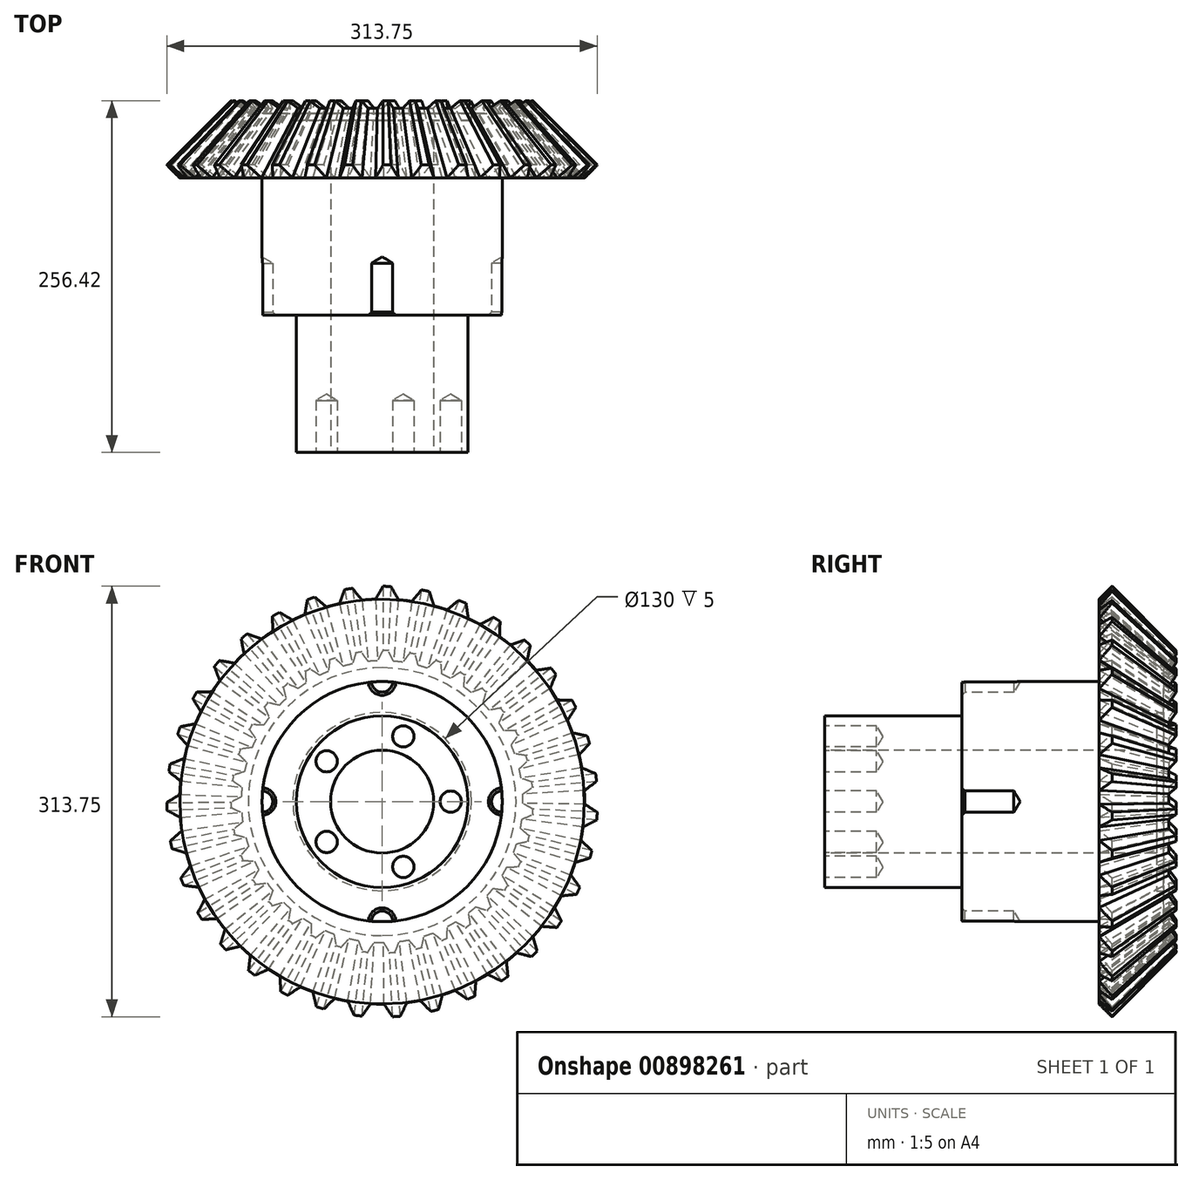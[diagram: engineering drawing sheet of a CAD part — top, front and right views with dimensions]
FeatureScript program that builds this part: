
annotation { "Feature Type Name" : "Feature", "Feature Type Description" : "" }
export const myFeature = defineFeature(function(context is Context, id is Id, definition is map)
    precondition{}
    {
        {
            var Q0;
            Q0=qCreatedBy(makeId("Front.planeOp"),FACE);
            var sketch = newSketch(context, id + "F0", { "sketchPlane" : qUnion([Q0])});
            skArc(sketch, "E0", {"start": v(-656.1, 368.1) * mm, "mid": v(-658.99, 367.13) * mm, "end": v(-661.85, 366.1) * mm});
            skLineSegment(sketch, "E1", {"start": v(-602.6, 62.21) * mm, "end": v(-595.9, 43.66) * mm});
            skLineSegment(sketch, "E2", {"start": v(-589.83, 44.07) * mm, "end": v(-586.01, 63.32) * mm});
            skLineSegment(sketch, "E3", {"start": v(-602.6, 62.21) * mm, "end": v(-604.03, 62.21) * mm});
            skLineSegment(sketch, "E4", {"start": v(-576.25, 64.84) * mm, "end": v(-566.34, 47.79) * mm});
            skLineSegment(sketch, "E5", {"start": v(-560.44, 49.27) * mm, "end": v(-560.12, 68.9) * mm});
            skLineSegment(sketch, "E6", {"start": v(-550.78, 72.14) * mm, "end": v(-537.98, 57.12) * mm});
            skLineSegment(sketch, "E7", {"start": v(-532.45, 59.64) * mm, "end": v(-535.64, 79) * mm});
            skLineSegment(sketch, "E8", {"start": v(-527.03, 83.86) * mm, "end": v(-511.75, 71.37) * mm});
            skLineSegment(sketch, "E9", {"start": v(-506.76, 74.83) * mm, "end": v(-513.35, 93.31) * mm});
            skLineSegment(sketch, "E10", {"start": v(-505.75, 99.63) * mm, "end": v(-488.5, 90.08) * mm});
            skLineSegment(sketch, "E11", {"start": v(-484.2, 94.37) * mm, "end": v(-493.98, 111.38) * mm});
            skLineSegment(sketch, "E12", {"start": v(-487.63, 118.96) * mm, "end": v(-468.94, 112.63) * mm});
            skLineSegment(sketch, "E13", {"start": v(-465.48, 117.63) * mm, "end": v(-478.14, 132.62) * mm});
            skLineSegment(sketch, "E14", {"start": v(-473.25, 141.2) * mm, "end": v(-453.73, 138.32) * mm});
            skLineSegment(sketch, "E15", {"start": v(-451.22, 143.85) * mm, "end": v(-466.36, 156.34) * mm});
            skLineSegment(sketch, "E16", {"start": v(-463.07, 165.66) * mm, "end": v(-443.36, 166.3) * mm});
            skLineSegment(sketch, "E17", {"start": v(-441.87, 172.2) * mm, "end": v(-459, 181.78) * mm});
            skLineSegment(sketch, "E18", {"start": v(-457.43, 191.54) * mm, "end": v(-438.14, 195.7) * mm});
            skLineSegment(sketch, "E19", {"start": v(-437.73, 201.76) * mm, "end": v(-456.3, 208.13) * mm});
            skLineSegment(sketch, "E20", {"start": v(-456.5, 218.01) * mm, "end": v(-438.26, 225.55) * mm});
            skLineSegment(sketch, "E21", {"start": v(-438.94, 231.59) * mm, "end": v(-458.34, 234.54) * mm});
            skLineSegment(sketch, "E22", {"start": v(-460.3, 244.23) * mm, "end": v(-443.7, 254.9) * mm});
            skLineSegment(sketch, "E23", {"start": v(-445.45, 260.72) * mm, "end": v(-465.07, 260.16) * mm});
            skLineSegment(sketch, "E24", {"start": v(-468.73, 269.34) * mm, "end": v(-454.3, 282.8) * mm});
            skLineSegment(sketch, "E25", {"start": v(-457.06, 288.22) * mm, "end": v(-476.26, 284.17) * mm});
            skLineSegment(sketch, "E26", {"start": v(-481.5, 292.55) * mm, "end": v(-469.72, 308.36) * mm});
            skLineSegment(sketch, "E27", {"start": v(-473.4, 313.2) * mm, "end": v(-491.57, 305.79) * mm});
            skLineSegment(sketch, "E28", {"start": v(-498.22, 313.1) * mm, "end": v(-489.45, 330.77) * mm});
            skLineSegment(sketch, "E29", {"start": v(-493.93, 334.87) * mm, "end": v(-510.48, 324.33) * mm});
            skLineSegment(sketch, "E30", {"start": v(-518.33, 330.33) * mm, "end": v(-512.86, 349.28) * mm});
            skLineSegment(sketch, "E31", {"start": v(-518, 352.52) * mm, "end": v(-532.4, 339.2) * mm});
            skLineSegment(sketch, "E32", {"start": v(-541.2, 343.7) * mm, "end": v(-539.2, 363.32) * mm});
            skLineSegment(sketch, "E33", {"start": v(-544.84, 365.59) * mm, "end": v(-556.63, 349.9) * mm});
            skLineSegment(sketch, "E34", {"start": v(-566.1, 352.77) * mm, "end": v(-567.62, 372.44) * mm});
            skLineSegment(sketch, "E35", {"start": v(-573.58, 373.66) * mm, "end": v(-582.38, 356.12) * mm});
            skLineSegment(sketch, "E36", {"start": v(-592.2, 357.25) * mm, "end": v(-597.22, 376.33) * mm});
            skLineSegment(sketch, "E37", {"start": v(-603.3, 376.46) * mm, "end": v(-608.83, 357.64) * mm});
            skLineSegment(sketch, "E38", {"start": v(-618.7, 357) * mm, "end": v(-627.03, 374.87) * mm});
            skLineSegment(sketch, "E39", {"start": v(-633.04, 373.92) * mm, "end": v(-635.12, 354.4) * mm});
            skLineSegment(sketch, "E40", {"start": v(-644.7, 352.01) * mm, "end": v(-656.1, 368.1) * mm});
            skLineSegment(sketch, "E41", {"start": v(-661.85, 366.1) * mm, "end": v(-660.4, 346.53) * mm});
            skLineSegment(sketch, "E42", {"start": v(-669.42, 342.47) * mm, "end": v(-683.51, 356.27) * mm});
            skLineSegment(sketch, "E43", {"start": v(-688.8, 353.27) * mm, "end": v(-683.89, 334.27) * mm});
            skLineSegment(sketch, "E44", {"start": v(-692.03, 328.66) * mm, "end": v(-708.36, 339.73) * mm});
            skLineSegment(sketch, "E45", {"start": v(-713.02, 335.83) * mm, "end": v(-704.8, 318.02) * mm});
            skLineSegment(sketch, "E46", {"start": v(-711.8, 311.04) * mm, "end": v(-729.85, 319.01) * mm});
            skLineSegment(sketch, "E47", {"start": v(-733.75, 314.35) * mm, "end": v(-722.48, 298.29) * mm});
            skLineSegment(sketch, "E48", {"start": v(-728.12, 290.17) * mm, "end": v(-747.3, 294.8) * mm});
            skLineSegment(sketch, "E49", {"start": v(-750.3, 289.5) * mm, "end": v(-736.34, 275.72) * mm});
            skLineSegment(sketch, "E50", {"start": v(-740.45, 266.73) * mm, "end": v(-760.14, 267.85) * mm});
            skLineSegment(sketch, "E51", {"start": v(-762.15, 262.11) * mm, "end": v(-745.96, 251.04) * mm});
            skLineSegment(sketch, "E52", {"start": v(-748.4, 241.46) * mm, "end": v(-767.97, 239.04) * mm});
            skLineSegment(sketch, "E53", {"start": v(-768.92, 233.04) * mm, "end": v(-751, 225.03) * mm});
            skLineSegment(sketch, "E54", {"start": v(-751.7, 215.17) * mm, "end": v(-770.53, 209.3) * mm});
            skLineSegment(sketch, "E55", {"start": v(-770.4, 203.23) * mm, "end": v(-751.34, 198.55) * mm});
            skLineSegment(sketch, "E56", {"start": v(-750.25, 188.72) * mm, "end": v(-767.73, 179.58) * mm});
            skLineSegment(sketch, "E57", {"start": v(-766.52, 173.63) * mm, "end": v(-746.93, 172.43) * mm});
            skLineSegment(sketch, "E58", {"start": v(-744.1, 162.95) * mm, "end": v(-759.68, 150.84) * mm});
            skLineSegment(sketch, "E59", {"start": v(-757.42, 145.2) * mm, "end": v(-737.93, 147.51) * mm});
            skLineSegment(sketch, "E60", {"start": v(-733.46, 138.7) * mm, "end": v(-746.62, 124) * mm});
            skLineSegment(sketch, "E61", {"start": v(-743.39, 118.85) * mm, "end": v(-724.63, 124.6) * mm});
            skLineSegment(sketch, "E62", {"start": v(-718.66, 116.73) * mm, "end": v(-728.98, 99.92) * mm});
            skLineSegment(sketch, "E63", {"start": v(-724.88, 95.43) * mm, "end": v(-707.45, 104.45) * mm});
            skLineSegment(sketch, "E64", {"start": v(-700.17, 97.76) * mm, "end": v(-707.32, 79.38) * mm});
            skLineSegment(sketch, "E65", {"start": v(-702.49, 75.7) * mm, "end": v(-686.95, 87.68) * mm});
            skLineSegment(sketch, "E66", {"start": v(-678.59, 82.4) * mm, "end": v(-682.35, 63.03) * mm});
            skLineSegment(sketch, "E67", {"start": v(-676.93, 60.27) * mm, "end": v(-663.78, 74.84) * mm});
            skLineSegment(sketch, "E68", {"start": v(-654.61, 71.14) * mm, "end": v(-654.85, 51.41) * mm});
            skLineSegment(sketch, "E69", {"start": v(-649.03, 49.66) * mm, "end": v(-638.7, 66.34) * mm});
            skLineSegment(sketch, "E70", {"start": v(-629.01, 64.34) * mm, "end": v(-625.72, 44.88) * mm});
            skLineSegment(sketch, "E71", {"start": v(-619.68, 44.2) * mm, "end": v(-612.49, 62.46) * mm});
            skArc(sketch, "E72", {"start": v(-683.51, 356.27) * mm, "mid": v(-686.17, 354.8) * mm, "end": v(-688.8, 353.27) * mm});
            skArc(sketch, "E73", {"start": v(-708.36, 339.73) * mm, "mid": v(-710.7, 337.8) * mm, "end": v(-713.02, 335.83) * mm});
            skArc(sketch, "E74", {"start": v(-729.85, 319.01) * mm, "mid": v(-731.82, 316.7) * mm, "end": v(-733.75, 314.35) * mm});
            skArc(sketch, "E75", {"start": v(-747.3, 294.8) * mm, "mid": v(-748.82, 292.16) * mm, "end": v(-750.3, 289.5) * mm});
            skArc(sketch, "E76", {"start": v(-760.14, 267.85) * mm, "mid": v(-761.17, 264.99) * mm, "end": v(-762.15, 262.11) * mm});
            skArc(sketch, "E77", {"start": v(-767.97, 239.04) * mm, "mid": v(-768.47, 236.05) * mm, "end": v(-768.92, 233.04) * mm});
            skArc(sketch, "E78", {"start": v(-770.53, 209.3) * mm, "mid": v(-770.49, 206.26) * mm, "end": v(-770.4, 203.23) * mm});
            skArc(sketch, "E79", {"start": v(-746.62, 124) * mm, "mid": v(-745.03, 121.41) * mm, "end": v(-743.39, 118.85) * mm});
            skArc(sketch, "E80", {"start": v(-759.68, 150.84) * mm, "mid": v(-758.57, 148.01) * mm, "end": v(-757.42, 145.2) * mm});
            skArc(sketch, "E81", {"start": v(-767.73, 179.58) * mm, "mid": v(-767.15, 176.6) * mm, "end": v(-766.52, 173.63) * mm});
            skArc(sketch, "E82", {"start": v(-728.98, 99.92) * mm, "mid": v(-726.95, 97.66) * mm, "end": v(-724.88, 95.43) * mm});
            skArc(sketch, "E83", {"start": v(-707.32, 79.38) * mm, "mid": v(-704.92, 77.51) * mm, "end": v(-702.49, 75.7) * mm});
            skArc(sketch, "E84", {"start": v(-682.35, 63.03) * mm, "mid": v(-679.65, 61.63) * mm, "end": v(-676.93, 60.27) * mm});
            skArc(sketch, "E85", {"start": v(-654.85, 51.41) * mm, "mid": v(-651.95, 50.5) * mm, "end": v(-649.03, 49.66) * mm});
            skArc(sketch, "E86", {"start": v(-625.72, 44.88) * mm, "mid": v(-622.7, 44.52) * mm, "end": v(-619.68, 44.2) * mm});
            skArc(sketch, "E87", {"start": v(-595.9, 43.66) * mm, "mid": v(-592.87, 43.84) * mm, "end": v(-589.83, 44.07) * mm});
            skArc(sketch, "E88", {"start": v(-566.34, 47.79) * mm, "mid": v(-563.38, 48.5) * mm, "end": v(-560.44, 49.27) * mm});
            skArc(sketch, "E89", {"start": v(-537.98, 57.12) * mm, "mid": v(-535.2, 58.36) * mm, "end": v(-532.45, 59.64) * mm});
            skArc(sketch, "E90", {"start": v(-511.75, 71.37) * mm, "mid": v(-509.24, 73.08) * mm, "end": v(-506.76, 74.83) * mm});
            skArc(sketch, "E91", {"start": v(-488.5, 90.08) * mm, "mid": v(-486.32, 92.2) * mm, "end": v(-484.2, 94.37) * mm});
            skArc(sketch, "E92", {"start": v(-468.94, 112.63) * mm, "mid": v(-467.19, 115.12) * mm, "end": v(-465.48, 117.63) * mm});
            skArc(sketch, "E93", {"start": v(-453.73, 138.32) * mm, "mid": v(-452.45, 141.07) * mm, "end": v(-451.22, 143.85) * mm});
            skArc(sketch, "E94", {"start": v(-443.36, 166.3) * mm, "mid": v(-442.59, 169.25) * mm, "end": v(-441.87, 172.2) * mm});
            skArc(sketch, "E95", {"start": v(-438.14, 195.7) * mm, "mid": v(-437.9, 198.73) * mm, "end": v(-437.73, 201.76) * mm});
            skArc(sketch, "E96", {"start": v(-438.26, 225.55) * mm, "mid": v(-438.57, 228.57) * mm, "end": v(-438.94, 231.59) * mm});
            skArc(sketch, "E97", {"start": v(-443.7, 254.9) * mm, "mid": v(-444.55, 257.82) * mm, "end": v(-445.45, 260.72) * mm});
            skArc(sketch, "E98", {"start": v(-454.3, 282.8) * mm, "mid": v(-455.66, 285.52) * mm, "end": v(-457.06, 288.22) * mm});
            skArc(sketch, "E99", {"start": v(-469.72, 308.36) * mm, "mid": v(-471.54, 310.8) * mm, "end": v(-473.4, 313.2) * mm});
            skArc(sketch, "E100", {"start": v(-489.45, 330.77) * mm, "mid": v(-491.67, 332.84) * mm, "end": v(-493.93, 334.87) * mm});
            skArc(sketch, "E101", {"start": v(-512.86, 349.28) * mm, "mid": v(-515.42, 350.93) * mm, "end": v(-518, 352.52) * mm});
            skArc(sketch, "E102", {"start": v(-539.2, 363.32) * mm, "mid": v(-542, 364.48) * mm, "end": v(-544.84, 365.59) * mm});
            skArc(sketch, "E103", {"start": v(-567.62, 372.44) * mm, "mid": v(-570.6, 373.07) * mm, "end": v(-573.58, 373.66) * mm});
            skArc(sketch, "E104", {"start": v(-597.22, 376.33) * mm, "mid": v(-600.62, 376.43) * mm, "end": v(-604.03, 376.46) * mm});
            skArc(sketch, "E105", {"start": v(-627.03, 374.87) * mm, "mid": v(-630.04, 374.42) * mm, "end": v(-633.04, 373.92) * mm});
            skArc(sketch, "E106", {"start": v(-510.48, 324.33) * mm, "mid": v(-514.36, 327.4) * mm, "end": v(-518.33, 330.33) * mm});
            skArc(sketch, "E107", {"start": v(-491.56, 305.79) * mm, "mid": v(-494.83, 309.5) * mm, "end": v(-498.22, 313.1) * mm});
            skArc(sketch, "E108", {"start": v(-476.26, 284.17) * mm, "mid": v(-478.81, 288.4) * mm, "end": v(-481.5, 292.55) * mm});
            skArc(sketch, "E109", {"start": v(-465.06, 260.16) * mm, "mid": v(-466.82, 264.78) * mm, "end": v(-468.73, 269.34) * mm});
            skArc(sketch, "E110", {"start": v(-532.4, 339.2) * mm, "mid": v(-536.77, 341.52) * mm, "end": v(-541.2, 343.7) * mm});
            skArc(sketch, "E111", {"start": v(-556.63, 349.91) * mm, "mid": v(-561.34, 351.42) * mm, "end": v(-566.1, 352.77) * mm});
            skArc(sketch, "E112", {"start": v(-582.38, 356.13) * mm, "mid": v(-587.28, 356.77) * mm, "end": v(-592.2, 357.25) * mm});
            skArc(sketch, "E113", {"start": v(-608.82, 357.64) * mm, "mid": v(-613.76, 357.4) * mm, "end": v(-618.7, 357) * mm});
            skArc(sketch, "E114", {"start": v(-635.12, 354.41) * mm, "mid": v(-639.93, 353.3) * mm, "end": v(-644.7, 352.01) * mm});
            skArc(sketch, "E115", {"start": v(-660.4, 346.54) * mm, "mid": v(-664.95, 344.58) * mm, "end": v(-669.42, 342.47) * mm});
            skArc(sketch, "E116", {"start": v(-683.9, 334.28) * mm, "mid": v(-688, 331.54) * mm, "end": v(-692.03, 328.66) * mm});
            skArc(sketch, "E117", {"start": v(-704.8, 318.02) * mm, "mid": v(-708.36, 314.6) * mm, "end": v(-711.8, 311.04) * mm});
            skArc(sketch, "E118", {"start": v(-722.48, 298.3) * mm, "mid": v(-725.37, 294.28) * mm, "end": v(-728.12, 290.17) * mm});
            skArc(sketch, "E119", {"start": v(-736.35, 275.72) * mm, "mid": v(-738.47, 271.26) * mm, "end": v(-740.45, 266.73) * mm});
            skArc(sketch, "E120", {"start": v(-745.96, 251.04) * mm, "mid": v(-747.26, 246.27) * mm, "end": v(-748.4, 241.46) * mm});
            skArc(sketch, "E121", {"start": v(-751.02, 225.04) * mm, "mid": v(-751.44, 220.11) * mm, "end": v(-751.7, 215.17) * mm});
            skArc(sketch, "E122", {"start": v(-751.34, 198.55) * mm, "mid": v(-750.88, 193.63) * mm, "end": v(-750.25, 188.72) * mm});
            skArc(sketch, "E123", {"start": v(-746.94, 172.43) * mm, "mid": v(-745.6, 167.67) * mm, "end": v(-744.1, 162.95) * mm});
            skArc(sketch, "E124", {"start": v(-737.94, 147.51) * mm, "mid": v(-735.78, 143.07) * mm, "end": v(-733.46, 138.7) * mm});
            skArc(sketch, "E125", {"start": v(-724.64, 124.6) * mm, "mid": v(-721.71, 120.62) * mm, "end": v(-718.66, 116.73) * mm});
            skArc(sketch, "E126", {"start": v(-707.46, 104.44) * mm, "mid": v(-703.87, 101.04) * mm, "end": v(-700.17, 97.76) * mm});
            skArc(sketch, "E127", {"start": v(-686.95, 87.67) * mm, "mid": v(-682.82, 84.97) * mm, "end": v(-678.59, 82.4) * mm});
            skArc(sketch, "E128", {"start": v(-663.79, 74.83) * mm, "mid": v(-659.23, 72.9) * mm, "end": v(-654.61, 71.14) * mm});
            skArc(sketch, "E129", {"start": v(-638.7, 66.33) * mm, "mid": v(-633.87, 65.25) * mm, "end": v(-629.01, 64.34) * mm});
            skArc(sketch, "E130", {"start": v(-612.5, 62.45) * mm, "mid": v(-607.55, 62.25) * mm, "end": v(-602.6, 62.21) * mm});
            skArc(sketch, "E131", {"start": v(-586.02, 63.3) * mm, "mid": v(-581.12, 64) * mm, "end": v(-576.25, 64.84) * mm});
            skArc(sketch, "E132", {"start": v(-560.12, 68.88) * mm, "mid": v(-555.42, 70.43) * mm, "end": v(-550.78, 72.14) * mm});
            skArc(sketch, "E133", {"start": v(-535.63, 79) * mm, "mid": v(-531.3, 81.35) * mm, "end": v(-527.03, 83.86) * mm});
            skArc(sketch, "E134", {"start": v(-513.35, 93.3) * mm, "mid": v(-509.5, 96.4) * mm, "end": v(-505.75, 99.63) * mm});
            skArc(sketch, "E135", {"start": v(-493.97, 111.37) * mm, "mid": v(-490.74, 115.11) * mm, "end": v(-487.63, 118.96) * mm});
            skArc(sketch, "E136", {"start": v(-478.14, 132.61) * mm, "mid": v(-475.62, 136.87) * mm, "end": v(-473.25, 141.2) * mm});
            skArc(sketch, "E137", {"start": v(-466.35, 156.33) * mm, "mid": v(-464.63, 160.97) * mm, "end": v(-463.07, 165.66) * mm});
            skArc(sketch, "E138", {"start": v(-458.99, 181.78) * mm, "mid": v(-458.12, 186.65) * mm, "end": v(-457.43, 191.54) * mm});
            skArc(sketch, "E139", {"start": v(-456.28, 208.13) * mm, "mid": v(-456.3, 213.07) * mm, "end": v(-456.5, 218.01) * mm});
            skArc(sketch, "E140", {"start": v(-458.33, 234.54) * mm, "mid": v(-459.23, 239.4) * mm, "end": v(-460.3, 244.23) * mm});
            skLineSegment(sketch, "E141", {"start": v(-605.28, 209.96) * mm, "end": v(-602.78, 209.96) * mm});
            skLineSegment(sketch, "E142", {"start": v(-604.03, 208.71) * mm, "end": v(-604.03, 211.21) * mm});
            skSolve(sketch);
        }
        {
            var Q0;
            {var subQ65=sQuery(id+"F0.wireOp",EDGE,"E0");Q0=makeQuery(id+"F0.imprint","IMPRINT",FACE,{"disambiguationData":[TD([[makeQuery(id+"F0.imprint","IMPRINT",EDGE,{"derivedFrom":subQ65}),1.0]])]});}
            cPlane(context, id + "F1", {"entities" : qUnion([Q0]), "cplaneType" : CPlaneType.OFFSET, "offset" : 56.57 * mm, "oppositeDirection" : true, "width" : 150 * mm, "height" : 150 * mm});
        }
        {
            var Q0;
            Q0=qCreatedBy(id+"F1.planeOp",FACE);
            var sketch = newSketch(context, id + "F2", { "sketchPlane" : qUnion([Q0])});
            skPoint(sketch, "E143.0", {"position": v(-604.03, 209.96) * mm});
            skCircle(sketch, "E144", {"center": v(-604.03, 209.96) * mm, "radius": 109.93 * mm, "construction": true});
            skArc(sketch, "E145", {"start": v(-607.2, 307.6) * mm, "mid": v(-610.46, 307.43) * mm, "end": v(-613.72, 307.16) * mm});
            skLineSegment(sketch, "E146", {"start": v(-596.21, 307.33) * mm, "end": v(-599.53, 319.8) * mm});
            skLineSegment(sketch, "E147", {"start": v(-603.55, 319.9) * mm, "end": v(-607.2, 307.6) * mm});
            skArc(sketch, "E148", {"start": v(-599.53, 319.8) * mm, "mid": v(-601.54, 319.87) * mm, "end": v(-603.55, 319.9) * mm});
            skArc(sketch, "E149.1.0", {"start": v(-619.22, 318.84) * mm, "mid": v(-621.2, 318.55) * mm, "end": v(-623.18, 318.21) * mm});
            skLineSegment(sketch, "E149.1.1", {"start": v(-623.18, 318.21) * mm, "end": v(-624.58, 305.46) * mm});
            skLineSegment(sketch, "E149.1.2", {"start": v(-613.72, 307.16) * mm, "end": v(-619.22, 318.84) * mm});
            skArc(sketch, "E149.2.0", {"start": v(-638.42, 314.38) * mm, "mid": v(-640.32, 313.73) * mm, "end": v(-642.2, 313.05) * mm});
            skLineSegment(sketch, "E149.2.1", {"start": v(-642.2, 313.05) * mm, "end": v(-641.3, 300.25) * mm});
            skLineSegment(sketch, "E149.2.2", {"start": v(-630.92, 303.87) * mm, "end": v(-638.42, 314.38) * mm});
            skArc(sketch, "E149.3.0", {"start": v(-656.5, 306.56) * mm, "mid": v(-658.26, 305.59) * mm, "end": v(-660, 304.58) * mm});
            skLineSegment(sketch, "E149.3.1", {"start": v(-660, 304.58) * mm, "end": v(-656.83, 292.15) * mm});
            skLineSegment(sketch, "E149.3.2", {"start": v(-647.26, 297.56) * mm, "end": v(-656.5, 306.56) * mm});
            skArc(sketch, "E149.4.0", {"start": v(-672.91, 295.64) * mm, "mid": v(-674.46, 294.37) * mm, "end": v(-676, 293.07) * mm});
            skLineSegment(sketch, "E149.4.1", {"start": v(-676, 293.07) * mm, "end": v(-670.65, 281.4) * mm});
            skLineSegment(sketch, "E149.4.2", {"start": v(-662.2, 288.43) * mm, "end": v(-672.91, 295.64) * mm});
            skArc(sketch, "E149.5.0", {"start": v(-687.1, 281.96) * mm, "mid": v(-688.4, 280.43) * mm, "end": v(-689.67, 278.88) * mm});
            skLineSegment(sketch, "E149.5.1", {"start": v(-689.67, 278.88) * mm, "end": v(-682.34, 268.36) * mm});
            skLineSegment(sketch, "E149.5.2", {"start": v(-675.28, 276.78) * mm, "end": v(-687.1, 281.96) * mm});
            skArc(sketch, "E149.6.0", {"start": v(-698.62, 265.97) * mm, "mid": v(-699.63, 264.24) * mm, "end": v(-700.6, 262.48) * mm});
            skLineSegment(sketch, "E149.6.1", {"start": v(-700.6, 262.48) * mm, "end": v(-691.5, 253.43) * mm});
            skLineSegment(sketch, "E149.6.2", {"start": v(-686.06, 262.99) * mm, "end": v(-698.62, 265.97) * mm});
            skArc(sketch, "E149.7.0", {"start": v(-707.1, 248.18) * mm, "mid": v(-707.78, 246.3) * mm, "end": v(-708.43, 244.4) * mm});
            skLineSegment(sketch, "E149.7.1", {"start": v(-708.43, 244.4) * mm, "end": v(-697.86, 237.12) * mm});
            skLineSegment(sketch, "E149.7.2", {"start": v(-694.21, 247.49) * mm, "end": v(-707.1, 248.18) * mm});
            skArc(sketch, "E149.8.0", {"start": v(-712.27, 229.16) * mm, "mid": v(-712.6, 227.18) * mm, "end": v(-712.9, 225.2) * mm});
            skLineSegment(sketch, "E149.8.1", {"start": v(-712.9, 225.2) * mm, "end": v(-701.2, 219.93) * mm});
            skLineSegment(sketch, "E149.8.2", {"start": v(-699.47, 230.78) * mm, "end": v(-712.27, 229.16) * mm});
            skArc(sketch, "E149.9.0", {"start": v(-713.96, 209.53) * mm, "mid": v(-713.93, 207.52) * mm, "end": v(-713.87, 205.52) * mm});
            skLineSegment(sketch, "E149.9.1", {"start": v(-713.87, 205.52) * mm, "end": v(-701.42, 202.42) * mm});
            skLineSegment(sketch, "E149.9.2", {"start": v(-701.65, 213.4) * mm, "end": v(-713.96, 209.53) * mm});
            skArc(sketch, "E149.10.0", {"start": v(-712.12, 189.9) * mm, "mid": v(-711.73, 187.94) * mm, "end": v(-711.31, 185.97) * mm});
            skLineSegment(sketch, "E149.10.1", {"start": v(-711.31, 185.97) * mm, "end": v(-698.5, 185.15) * mm});
            skLineSegment(sketch, "E149.10.2", {"start": v(-700.7, 195.92) * mm, "end": v(-712.12, 189.9) * mm});
            skArc(sketch, "E149.11.0", {"start": v(-706.8, 170.93) * mm, "mid": v(-706.07, 169.06) * mm, "end": v(-705.3, 167.2) * mm});
            skLineSegment(sketch, "E149.11.1", {"start": v(-705.3, 167.2) * mm, "end": v(-692.56, 168.68) * mm});
            skLineSegment(sketch, "E149.11.2", {"start": v(-696.63, 178.89) * mm, "end": v(-706.8, 170.93) * mm});
            skArc(sketch, "E149.12.0", {"start": v(-698.18, 153.2) * mm, "mid": v(-697.12, 151.5) * mm, "end": v(-696.04, 149.8) * mm});
            skLineSegment(sketch, "E149.12.1", {"start": v(-696.04, 149.8) * mm, "end": v(-683.76, 153.53) * mm});
            skLineSegment(sketch, "E149.12.2", {"start": v(-689.6, 162.85) * mm, "end": v(-698.18, 153.2) * mm});
            skArc(sketch, "E149.13.0", {"start": v(-686.53, 137.3) * mm, "mid": v(-685.19, 135.81) * mm, "end": v(-683.82, 134.35) * mm});
            skLineSegment(sketch, "E149.13.1", {"start": v(-683.82, 134.35) * mm, "end": v(-672.4, 140.2) * mm});
            skLineSegment(sketch, "E149.13.2", {"start": v(-679.8, 148.33) * mm, "end": v(-686.53, 137.3) * mm});
            skArc(sketch, "E149.14.0", {"start": v(-672.23, 123.75) * mm, "mid": v(-670.64, 122.52) * mm, "end": v(-669.04, 121.31) * mm});
            skLineSegment(sketch, "E149.14.1", {"start": v(-669.04, 121.31) * mm, "end": v(-658.85, 129.12) * mm});
            skLineSegment(sketch, "E149.14.2", {"start": v(-667.59, 135.79) * mm, "end": v(-672.23, 123.75) * mm});
            skArc(sketch, "E149.15.0", {"start": v(-655.74, 112.95) * mm, "mid": v(-653.96, 112.03) * mm, "end": v(-652.16, 111.13) * mm});
            skLineSegment(sketch, "E149.15.1", {"start": v(-652.16, 111.13) * mm, "end": v(-643.53, 120.63) * mm});
            skLineSegment(sketch, "E149.15.2", {"start": v(-653.32, 125.63) * mm, "end": v(-655.74, 112.95) * mm});
            skArc(sketch, "E149.16.0", {"start": v(-637.58, 105.28) * mm, "mid": v(-635.67, 104.68) * mm, "end": v(-633.74, 104.12) * mm});
            skLineSegment(sketch, "E149.16.1", {"start": v(-633.74, 104.12) * mm, "end": v(-626.95, 115.01) * mm});
            skLineSegment(sketch, "E149.16.2", {"start": v(-637.47, 118.19) * mm, "end": v(-637.58, 105.28) * mm});
            skArc(sketch, "E149.17.0", {"start": v(-618.35, 100.97) * mm, "mid": v(-616.36, 100.73) * mm, "end": v(-614.37, 100.52) * mm});
            skLineSegment(sketch, "E149.17.1", {"start": v(-614.37, 100.52) * mm, "end": v(-609.62, 112.44) * mm});
            skLineSegment(sketch, "E149.17.2", {"start": v(-620.55, 113.7) * mm, "end": v(-618.35, 100.97) * mm});
            skArc(sketch, "E149.18.0", {"start": v(-598.66, 100.16) * mm, "mid": v(-596.66, 100.28) * mm, "end": v(-594.66, 100.43) * mm});
            skLineSegment(sketch, "E149.18.1", {"start": v(-594.66, 100.43) * mm, "end": v(-592.12, 113.01) * mm});
            skLineSegment(sketch, "E149.18.2", {"start": v(-603.09, 112.29) * mm, "end": v(-598.66, 100.16) * mm});
            skArc(sketch, "E149.19.0", {"start": v(-579.14, 102.89) * mm, "mid": v(-577.2, 103.36) * mm, "end": v(-575.25, 103.87) * mm});
            skLineSegment(sketch, "E149.19.1", {"start": v(-575.25, 103.87) * mm, "end": v(-575, 116.7) * mm});
            skLineSegment(sketch, "E149.19.2", {"start": v(-585.66, 114.03) * mm, "end": v(-579.14, 102.89) * mm});
            skArc(sketch, "E149.20.0", {"start": v(-560.42, 109.05) * mm, "mid": v(-558.59, 109.87) * mm, "end": v(-556.77, 110.71) * mm});
            skLineSegment(sketch, "E149.20.1", {"start": v(-556.77, 110.71) * mm, "end": v(-558.81, 123.38) * mm});
            skLineSegment(sketch, "E149.20.2", {"start": v(-568.83, 118.85) * mm, "end": v(-560.42, 109.05) * mm});
            skArc(sketch, "E149.21.0", {"start": v(-543.1, 118.46) * mm, "mid": v(-541.45, 119.59) * mm, "end": v(-539.8, 120.74) * mm});
            skLineSegment(sketch, "E149.21.1", {"start": v(-539.8, 120.74) * mm, "end": v(-544.08, 132.85) * mm});
            skLineSegment(sketch, "E149.21.2", {"start": v(-553.13, 126.6) * mm, "end": v(-543.1, 118.46) * mm});
            skArc(sketch, "E149.22.0", {"start": v(-527.75, 130.8) * mm, "mid": v(-526.31, 132.21) * mm, "end": v(-524.9, 133.65) * mm});
            skLineSegment(sketch, "E149.22.1", {"start": v(-524.9, 133.65) * mm, "end": v(-531.27, 144.79) * mm});
            skLineSegment(sketch, "E149.22.2", {"start": v(-539.06, 137.03) * mm, "end": v(-527.75, 130.8) * mm});
            skArc(sketch, "E149.23.0", {"start": v(-514.84, 145.7) * mm, "mid": v(-513.68, 147.34) * mm, "end": v(-512.55, 149) * mm});
            skLineSegment(sketch, "E149.23.1", {"start": v(-512.55, 149) * mm, "end": v(-520.8, 158.83) * mm});
            skLineSegment(sketch, "E149.23.2", {"start": v(-527.08, 149.8) * mm, "end": v(-514.84, 145.7) * mm});
            skArc(sketch, "E149.24.0", {"start": v(-504.8, 162.66) * mm, "mid": v(-503.95, 164.48) * mm, "end": v(-503.14, 166.31) * mm});
            skLineSegment(sketch, "E149.24.1", {"start": v(-503.14, 166.31) * mm, "end": v(-513.01, 174.51) * mm});
            skLineSegment(sketch, "E149.24.2", {"start": v(-517.57, 164.5) * mm, "end": v(-504.8, 162.66) * mm});
            skArc(sketch, "E149.25.0", {"start": v(-497.95, 181.14) * mm, "mid": v(-497.44, 183.08) * mm, "end": v(-496.96, 185.03) * mm});
            skLineSegment(sketch, "E149.25.1", {"start": v(-496.96, 185.03) * mm, "end": v(-508.14, 191.33) * mm});
            skLineSegment(sketch, "E149.25.2", {"start": v(-510.84, 180.68) * mm, "end": v(-497.95, 181.14) * mm});
            skArc(sketch, "E149.26.0", {"start": v(-494.5, 200.55) * mm, "mid": v(-494.35, 202.55) * mm, "end": v(-494.23, 204.55) * mm});
            skLineSegment(sketch, "E149.26.1", {"start": v(-494.23, 204.55) * mm, "end": v(-506.36, 208.75) * mm});
            skLineSegment(sketch, "E149.26.2", {"start": v(-507.11, 197.78) * mm, "end": v(-494.5, 200.55) * mm});
            skArc(sketch, "E149.27.0", {"start": v(-494.58, 220.25) * mm, "mid": v(-494.79, 222.25) * mm, "end": v(-495.03, 224.24) * mm});
            skLineSegment(sketch, "E149.27.1", {"start": v(-495.03, 224.24) * mm, "end": v(-507.71, 226.21) * mm});
            skLineSegment(sketch, "E149.27.2", {"start": v(-506.5, 215.29) * mm, "end": v(-494.58, 220.25) * mm});
            skArc(sketch, "E149.28.0", {"start": v(-498.18, 239.63) * mm, "mid": v(-498.74, 241.56) * mm, "end": v(-499.33, 243.47) * mm});
            skLineSegment(sketch, "E149.28.1", {"start": v(-499.33, 243.47) * mm, "end": v(-512.16, 243.15) * mm});
            skLineSegment(sketch, "E149.28.2", {"start": v(-509.01, 232.62) * mm, "end": v(-498.18, 239.63) * mm});
            skArc(sketch, "E149.29.0", {"start": v(-505.18, 258.05) * mm, "mid": v(-506.07, 259.85) * mm, "end": v(-507, 261.63) * mm});
            skLineSegment(sketch, "E149.29.1", {"start": v(-507, 261.63) * mm, "end": v(-519.56, 259.02) * mm});
            skLineSegment(sketch, "E149.29.2", {"start": v(-514.58, 249.22) * mm, "end": v(-505.18, 258.05) * mm});
            skArc(sketch, "E149.30.0", {"start": v(-515.35, 274.93) * mm, "mid": v(-516.55, 276.54) * mm, "end": v(-517.78, 278.13) * mm});
            skLineSegment(sketch, "E149.30.1", {"start": v(-517.78, 278.13) * mm, "end": v(-529.68, 273.31) * mm});
            skLineSegment(sketch, "E149.30.2", {"start": v(-523.03, 264.56) * mm, "end": v(-515.35, 274.93) * mm});
            skArc(sketch, "E149.31.0", {"start": v(-528.38, 289.72) * mm, "mid": v(-529.85, 291.1) * mm, "end": v(-531.34, 292.43) * mm});
            skLineSegment(sketch, "E149.31.1", {"start": v(-531.34, 292.43) * mm, "end": v(-542.18, 285.57) * mm});
            skLineSegment(sketch, "E149.31.2", {"start": v(-534.08, 278.14) * mm, "end": v(-528.38, 289.72) * mm});
            skArc(sketch, "E149.32.0", {"start": v(-543.83, 301.95) * mm, "mid": v(-545.52, 303.03) * mm, "end": v(-547.23, 304.09) * mm});
            skLineSegment(sketch, "E149.32.1", {"start": v(-547.23, 304.09) * mm, "end": v(-556.68, 295.4) * mm});
            skLineSegment(sketch, "E149.32.2", {"start": v(-547.38, 289.54) * mm, "end": v(-543.83, 301.95) * mm});
            skArc(sketch, "E149.33.0", {"start": v(-561.23, 311.22) * mm, "mid": v(-563.08, 311.98) * mm, "end": v(-564.95, 312.71) * mm});
            skLineSegment(sketch, "E149.33.1", {"start": v(-564.95, 312.71) * mm, "end": v(-572.7, 302.48) * mm});
            skLineSegment(sketch, "E149.33.2", {"start": v(-562.5, 298.37) * mm, "end": v(-561.23, 311.22) * mm});
            skArc(sketch, "E149.34.0", {"start": v(-580, 317.24) * mm, "mid": v(-581.96, 317.66) * mm, "end": v(-583.93, 318.04) * mm});
            skLineSegment(sketch, "E149.34.1", {"start": v(-583.93, 318.04) * mm, "end": v(-589.72, 306.6) * mm});
            skLineSegment(sketch, "E149.34.2", {"start": v(-578.95, 304.37) * mm, "end": v(-580, 317.24) * mm});
            skArc(sketch, "E150.trimOffspring", {"start": v(-624.58, 305.46) * mm, "mid": v(-627.77, 304.72) * mm, "end": v(-630.92, 303.87) * mm});
            skArc(sketch, "E151.trimOffspring", {"start": v(-641.3, 300.25) * mm, "mid": v(-644.3, 298.96) * mm, "end": v(-647.26, 297.56) * mm});
            skArc(sketch, "E152.trimOffspring", {"start": v(-656.83, 292.15) * mm, "mid": v(-659.55, 290.34) * mm, "end": v(-662.2, 288.43) * mm});
            skArc(sketch, "E153.trimOffspring", {"start": v(-670.65, 281.4) * mm, "mid": v(-673, 279.13) * mm, "end": v(-675.28, 276.78) * mm});
            skArc(sketch, "E154.trimOffspring", {"start": v(-682.34, 268.36) * mm, "mid": v(-684.25, 265.7) * mm, "end": v(-686.06, 262.99) * mm});
            skArc(sketch, "E155.trimOffspring", {"start": v(-691.5, 253.43) * mm, "mid": v(-692.9, 250.48) * mm, "end": v(-694.21, 247.49) * mm});
            skArc(sketch, "E156.trimOffspring", {"start": v(-697.86, 237.12) * mm, "mid": v(-698.72, 233.96) * mm, "end": v(-699.47, 230.78) * mm});
            skArc(sketch, "E157.trimOffspring", {"start": v(-701.2, 219.93) * mm, "mid": v(-701.48, 216.67) * mm, "end": v(-701.65, 213.4) * mm});
            skArc(sketch, "E158.trimOffspring", {"start": v(-589.72, 306.6) * mm, "mid": v(-592.96, 307.01) * mm, "end": v(-596.21, 307.33) * mm});
            skArc(sketch, "E159.trimOffspring", {"start": v(-572.7, 302.48) * mm, "mid": v(-575.8, 303.48) * mm, "end": v(-578.95, 304.37) * mm});
            skArc(sketch, "E160.trimOffspring", {"start": v(-556.68, 295.4) * mm, "mid": v(-559.56, 296.94) * mm, "end": v(-562.5, 298.37) * mm});
            skArc(sketch, "E161.trimOffspring", {"start": v(-542.18, 285.57) * mm, "mid": v(-544.75, 287.6) * mm, "end": v(-547.38, 289.54) * mm});
            skArc(sketch, "E162.trimOffspring", {"start": v(-529.68, 273.31) * mm, "mid": v(-531.84, 275.77) * mm, "end": v(-534.08, 278.14) * mm});
            skArc(sketch, "E163.trimOffspring", {"start": v(-519.56, 259.02) * mm, "mid": v(-521.25, 261.82) * mm, "end": v(-523.03, 264.56) * mm});
            skArc(sketch, "E164.trimOffspring", {"start": v(-512.16, 243.15) * mm, "mid": v(-513.32, 246.2) * mm, "end": v(-514.58, 249.22) * mm});
            skArc(sketch, "E165.trimOffspring", {"start": v(-507.71, 226.21) * mm, "mid": v(-508.3, 229.42) * mm, "end": v(-509.01, 232.62) * mm});
            skArc(sketch, "E166.trimOffspring", {"start": v(-506.36, 208.75) * mm, "mid": v(-506.37, 212.02) * mm, "end": v(-506.5, 215.29) * mm});
            skArc(sketch, "E167.trimOffspring", {"start": v(-508.14, 191.33) * mm, "mid": v(-507.57, 194.55) * mm, "end": v(-507.11, 197.78) * mm});
            skArc(sketch, "E168.trimOffspring", {"start": v(-513.01, 174.51) * mm, "mid": v(-511.88, 177.57) * mm, "end": v(-510.84, 180.68) * mm});
            skArc(sketch, "E169.trimOffspring", {"start": v(-520.8, 158.83) * mm, "mid": v(-519.14, 161.64) * mm, "end": v(-517.57, 164.5) * mm});
            skArc(sketch, "E170.trimOffspring", {"start": v(-531.27, 144.79) * mm, "mid": v(-529.13, 147.26) * mm, "end": v(-527.08, 149.8) * mm});
            skArc(sketch, "E171.trimOffspring", {"start": v(-544.08, 132.85) * mm, "mid": v(-541.53, 134.9) * mm, "end": v(-539.06, 137.03) * mm});
            skArc(sketch, "E172.trimOffspring", {"start": v(-558.81, 123.38) * mm, "mid": v(-555.94, 124.94) * mm, "end": v(-553.13, 126.6) * mm});
            skArc(sketch, "E173.trimOffspring", {"start": v(-575, 116.7) * mm, "mid": v(-571.9, 117.72) * mm, "end": v(-568.83, 118.85) * mm});
            skArc(sketch, "E174.trimOffspring", {"start": v(-592.12, 113.01) * mm, "mid": v(-588.88, 113.47) * mm, "end": v(-585.66, 114.03) * mm});
            skArc(sketch, "E175.trimOffspring", {"start": v(-609.62, 112.44) * mm, "mid": v(-606.36, 112.31) * mm, "end": v(-603.09, 112.29) * mm});
            skArc(sketch, "E176.trimOffspring", {"start": v(-626.95, 115.01) * mm, "mid": v(-623.76, 114.3) * mm, "end": v(-620.55, 113.7) * mm});
            skArc(sketch, "E177.trimOffspring", {"start": v(-643.53, 120.63) * mm, "mid": v(-640.52, 119.36) * mm, "end": v(-637.47, 118.19) * mm});
            skArc(sketch, "E178.trimOffspring", {"start": v(-658.85, 129.12) * mm, "mid": v(-656.11, 127.33) * mm, "end": v(-653.32, 125.63) * mm});
            skArc(sketch, "E179.trimOffspring", {"start": v(-672.4, 140.2) * mm, "mid": v(-670.03, 137.96) * mm, "end": v(-667.59, 135.79) * mm});
            skArc(sketch, "E180.trimOffspring", {"start": v(-683.76, 153.53) * mm, "mid": v(-681.83, 150.9) * mm, "end": v(-679.8, 148.33) * mm});
            skArc(sketch, "E181.trimOffspring", {"start": v(-692.56, 168.68) * mm, "mid": v(-691.12, 165.74) * mm, "end": v(-689.6, 162.85) * mm});
            skArc(sketch, "E182.trimOffspring", {"start": v(-698.5, 185.15) * mm, "mid": v(-697.62, 182) * mm, "end": v(-696.63, 178.89) * mm});
            skArc(sketch, "E183.trimOffspring", {"start": v(-701.42, 202.42) * mm, "mid": v(-701.11, 199.16) * mm, "end": v(-700.7, 195.92) * mm});
            skSolve(sketch);
        }
        {
            var Q0;
            Q0 = qSketchRegion(id + "F0", true);
            var Q1;
            Q1 = qSketchRegion(id + "F2", true);
            loft(context, id + "F3", {"sheetProfilesArray" : [{ "sheetProfileEntities" : qUnion([Q0]) }, { "sheetProfileEntities" : qUnion([Q1]) }]});
        }
        {
            var Q0;
            {var subQ65=sQuery(id+"F0.wireOp",EDGE,"E0");Q0=makeQuery(id+"F3.opLoft","SWEPT_BODY",BODY,{"disambiguationData":[OSD([makeQuery(id+"F0.imprint","IMPRINT",FACE,{"disambiguationData":[TD([[makeQuery(id+"F0.imprint","IMPRINT",EDGE,{"derivedFrom":subQ65}),1.0]])]}),makeQuery(id+"F2.imprint","IMPRINT",FACE,{"disambiguationData":[TD([[makeQuery(id+"F2.imprint","IMPRINT",EDGE,{"derivedFrom":sQuery(id+"F2.wireOp",EDGE,"E145")}),1.0]])]})])]});}
            transform(context, id + "F4", {"entities" : qUnion([Q0]), "transformType" : TransformType.TRANSLATION_3D, "dx" : 604.03 * mm, "dy" : 0 * mm, "dz" : 0 * mm, "makeCopy" : false});
        }
        {
            var Q0;
            {var subQ65=sQuery(id+"F0.wireOp",EDGE,"E0");Q0=makeQuery(id+"F3.opLoft","SWEPT_BODY",BODY,{"disambiguationData":[OSD([makeQuery(id+"F0.imprint","IMPRINT",FACE,{"disambiguationData":[TD([[makeQuery(id+"F0.imprint","IMPRINT",EDGE,{"derivedFrom":subQ65}),1.0]])]}),makeQuery(id+"F2.imprint","IMPRINT",FACE,{"disambiguationData":[TD([[makeQuery(id+"F2.imprint","IMPRINT",EDGE,{"derivedFrom":sQuery(id+"F2.wireOp",EDGE,"E145")}),1.0]])]})])]});}
            transform(context, id + "F5", {"entities" : qUnion([Q0]), "transformType" : TransformType.TRANSLATION_3D, "dx" : 0 * mm, "dy" : 0 * mm, "dz" : -209.96 * mm, "makeCopy" : false});
        }
        {
            var Q0;
            Q0=qCreatedBy(makeId("Right.planeOp"),FACE);
            var sketch = newSketch(context, id + "F6", { "sketchPlane" : qUnion([Q0])});
            skPoint(sketch, "E184.0", {"position": v(0, 147.44) * mm});
            skPoint(sketch, "E185.0", {"position": v(56.57, 97.63) * mm});
            skLineSegment(sketch, "E186", {"start": v(66.28, 123.34) * mm, "end": v(47.15, 97.63) * mm});
            skLineSegment(sketch, "E187", {"start": v(47.15, 97.63) * mm, "end": v(66.28, 97.63) * mm});
            skLineSegment(sketch, "E188", {"start": v(66.28, 97.63) * mm, "end": v(66.28, 123.34) * mm});
            skLineSegment(sketch, "E189", {"start": v(0, 147.44) * mm, "end": v(41.56, 189) * mm});
            skLineSegment(sketch, "E190", {"start": v(41.56, 189) * mm, "end": v(0, 189) * mm});
            skLineSegment(sketch, "E191", {"start": v(0, 189) * mm, "end": v(0, 147.44) * mm});
            skLineSegment(sketch, "E192.bottom", {"start": v(66.28, 97.63) * mm, "end": v(47.15, 97.63) * mm, "construction": true});
            skLineSegment(sketch, "E192.top", {"start": v(66.28, 0) * mm, "end": v(47.15, 0) * mm});
            skLineSegment(sketch, "E192.left", {"start": v(66.28, 97.63) * mm, "end": v(66.28, 0) * mm});
            skLineSegment(sketch, "E192.right", {"start": v(47.15, 97.63) * mm, "end": v(47.15, 0) * mm});
            skSolve(sketch);
        }
        {
            var Q0;
            Q0=makeQuery(id+"F6.imprint","IMPRINT",FACE,{"disambiguationData":[TD([[makeQuery(id+"F6.imprint","IMPRINT",EDGE,{"derivedFrom":sQuery(id+"F6.wireOp",EDGE,"E189")}),1.0]])]});
            var Q1;
            Q1=makeQuery(id+"F6.imprint","IMPRINT",FACE,{"disambiguationData":[TD([[makeQuery(id+"F6.imprint","IMPRINT",EDGE,{"derivedFrom":sQuery(id+"F6.wireOp",EDGE,"E187")}),-1.0]])]});
            var Q2;
            Q2=makeQuery(id+"F6.imprint","IMPRINT",FACE,{"disambiguationData":[TD([[makeQuery(id+"F6.imprint","IMPRINT",EDGE,{"derivedFrom":sQuery(id+"F6.wireOp",EDGE,"E186")}),1.0]])]});
            var Q3;
            Q3=sQuery(id+"F6.wireOp",EDGE,"E192.top");
            revolve(context, id + "F7", {"operationType" : NewBodyOperationType.REMOVE, "surfaceOperationType" : NewSurfaceOperationType.NEW, "entities" : qUnion([Q0, Q1, Q2]), "axis" : qUnion([Q3]), "revolveType" : RevolveType.FULL, "oppositeDirection" : true});
        }
        {
            var Q0;
            {var subQ65=sQuery(id+"F0.wireOp",EDGE,"E0");Q0=makeQuery(id+"F3.opLoft","CAP_FACE",FACE,{"disambiguationData":[OSD([makeQuery(id+"F0.imprint","IMPRINT",FACE,{"disambiguationData":[TD([[makeQuery(id+"F0.imprint","IMPRINT",EDGE,{"derivedFrom":subQ65}),1.0]])]})])],"isStart":true});}
            var sketch = newSketch(context, id + "F8", { "sketchPlane" : qUnion([Q0])});
            skCircle(sketch, "E193", {"center": v(0, 0) * mm, "radius": 87.5 * mm});
            skSolve(sketch);
        }
        {
            var Q0;
            Q0=makeQuery(id+"F8.imprint","IMPRINT",FACE,{"disambiguationData":[TD([[makeQuery(id+"F8.imprint","IMPRINT",EDGE,{"derivedFrom":sQuery(id+"F8.wireOp",EDGE,"E193")}),1.0]])]});
            extrude(context, id + "F9", {"entities" : qUnion([Q0]), "operationType" : NewBodyOperationType.ADD, "depth" : 100 * mm, "offsetDistance" : 25 * mm});
        }
        {
            var Q0;
            Q0=makeQuery(id+"F9.opExtrude","CAP_FACE",FACE,{"disambiguationData":[OSD([sQuery(id+"F8.wireOp",EDGE,"E193")])],"isStart":false});
            var sketch = newSketch(context, id + "F10", { "sketchPlane" : qUnion([Q0])});
            skCircle(sketch, "E194", {"center": v(0, 0) * mm, "radius": 62.5 * mm});
            skSolve(sketch);
        }
        {
            var Q0;
            Q0=makeQuery(id+"F10.imprint","IMPRINT",FACE,{"disambiguationData":[TD([[makeQuery(id+"F10.imprint","IMPRINT",EDGE,{"derivedFrom":sQuery(id+"F10.wireOp",EDGE,"E194")}),1.0]])]});
            extrude(context, id + "F11", {"entities" : qUnion([Q0]), "operationType" : NewBodyOperationType.ADD, "depth" : 100 * mm, "offsetDistance" : 25 * mm});
        }
        {
            var Q0;
            Q0=makeQuery(id+"F11.opExtrude","CAP_FACE",FACE,{"disambiguationData":[OSD([sQuery(id+"F10.wireOp",EDGE,"E194")])],"isStart":false});
            var sketch = newSketch(context, id + "F12", { "sketchPlane" : qUnion([Q0])});
            skCircle(sketch, "E195", {"center": v(0, 0) * mm, "radius": 37.5 * mm});
            skSolve(sketch);
        }
        {
            var Q0;
            Q0=makeQuery(id+"F12.imprint","IMPRINT",FACE,{"disambiguationData":[TD([[makeQuery(id+"F12.imprint","IMPRINT",EDGE,{"derivedFrom":sQuery(id+"F12.wireOp",EDGE,"E195")}),1.0]])]});
            extrude(context, id + "F13", {"entities" : qUnion([Q0]), "operationType" : NewBodyOperationType.REMOVE, "endBound" : BoundingType.THROUGH_ALL, "oppositeDirection" : true, "depth" : 25 * mm, "offsetDistance" : 25 * mm});
        }
        {
            var Q0;
            Q0=makeQuery(id+"F9.opExtrude","CAP_FACE",FACE,{"disambiguationData":[OSD([sQuery(id+"F8.wireOp",EDGE,"E193")])],"isStart":false});
            var sketch = newSketch(context, id + "F14", { "sketchPlane" : qUnion([Q0])});
            skPoint(sketch, "E196", {"position": v(87.5, 0) * mm});
            skPoint(sketch, "E197", {"position": v(0, 87.5) * mm});
            skPoint(sketch, "E198", {"position": v(-87.5, 0) * mm});
            skPoint(sketch, "E199", {"position": v(0, -87.5) * mm});
            skSolve(sketch);
        }
        {
            var Q0;
            Q0=sQuery(id+"F14.wireOp",VERTEX,"E197");
            var Q1;
            Q1=sQuery(id+"F14.wireOp",VERTEX,"E198");
            var Q2;
            Q2=sQuery(id+"F14.wireOp",VERTEX,"E199");
            var Q3;
            Q3=sQuery(id+"F14.wireOp",VERTEX,"E196");
            var Q4;
            {var subQ65=sQuery(id+"F0.wireOp",EDGE,"E0");Q4=makeQuery(id+"F3.opLoft","SWEPT_BODY",BODY,{"disambiguationData":[OSD([makeQuery(id+"F0.imprint","IMPRINT",FACE,{"disambiguationData":[TD([[makeQuery(id+"F0.imprint","IMPRINT",EDGE,{"derivedFrom":subQ65}),1.0]])]}),makeQuery(id+"F2.imprint","IMPRINT",FACE,{"disambiguationData":[TD([[makeQuery(id+"F2.imprint","IMPRINT",EDGE,{"derivedFrom":sQuery(id+"F2.wireOp",EDGE,"E145")}),1.0]])]})])]});}
            hole(context, id + "F15", {"style" : HoleStyle.C_SINK, "endStyle" : HoleEndStyle.BLIND, "holeDiameter" : 15.5 * mm, "cSinkDiameter" : 20 * mm, "cSinkAngle" : 90 * degree, "majorDiameter" : 5 * mm, "holeDepth" : 38 * mm, "isTappedThrough" : true, "tappedDepth" : 12 * mm, "tapClearance" : 3, "startFromSketch" : true, "locations" : qUnion([Q0, Q1, Q2, Q3]), "scope" : qUnion([Q4])});
        }
        {
            var Q0;
            Q0=makeQuery(id+"F11.opExtrude","CAP_FACE",FACE,{"disambiguationData":[OSD([sQuery(id+"F10.wireOp",EDGE,"E194")])],"isStart":false});
            var sketch = newSketch(context, id + "F16", { "sketchPlane" : qUnion([Q0])});
            skPoint(sketch, "E200", {"position": v(50, 0) * mm});
            skPoint(sketch, "E201.1.0", {"position": v(15.45, 47.55) * mm});
            skPoint(sketch, "E201.2.0", {"position": v(-40.45, 29.39) * mm});
            skPoint(sketch, "E201.3.0", {"position": v(-40.45, -29.39) * mm});
            skPoint(sketch, "E201.4.0", {"position": v(15.45, -47.55) * mm});
            skPoint(sketch, "E201.center", {"position": v(0, 0) * mm});
            skSolve(sketch);
        }
        {
            var Q0;
            Q0=sQuery(id+"F16.wireOp",VERTEX,"E201.1.0");
            var Q1;
            Q1=sQuery(id+"F16.wireOp",VERTEX,"E201.2.0");
            var Q2;
            Q2=sQuery(id+"F16.wireOp",VERTEX,"E201.3.0");
            var Q3;
            Q3=sQuery(id+"F16.wireOp",VERTEX,"E201.4.0");
            var Q4;
            Q4=sQuery(id+"F16.wireOp",VERTEX,"E200");
            var Q5;
            {var subQ65=sQuery(id+"F0.wireOp",EDGE,"E0");Q5=makeQuery(id+"F3.opLoft","SWEPT_BODY",BODY,{"disambiguationData":[OSD([makeQuery(id+"F0.imprint","IMPRINT",FACE,{"disambiguationData":[TD([[makeQuery(id+"F0.imprint","IMPRINT",EDGE,{"derivedFrom":subQ65}),1.0]])]}),makeQuery(id+"F2.imprint","IMPRINT",FACE,{"disambiguationData":[TD([[makeQuery(id+"F2.imprint","IMPRINT",EDGE,{"derivedFrom":sQuery(id+"F2.wireOp",EDGE,"E145")}),1.0]])]})])]});}
            hole(context, id + "F17", {"style" : HoleStyle.SIMPLE, "endStyle" : HoleEndStyle.BLIND, "holeDiameter" : 15.5 * mm, "majorDiameter" : 5 * mm, "holeDepth" : 38 * mm, "isTappedThrough" : true, "tappedDepth" : 12 * mm, "tapClearance" : 3, "startFromSketch" : true, "locations" : qUnion([Q0, Q1, Q2, Q3, Q4]), "scope" : qUnion([Q5])});
        }
        {
            var Q0;
            Q0=makeQuery(id+"F7.boolean.opBoolean","COPY",FACE,{"derivedFrom":makeQuery(id+"F7.opRevolve","SWEPT_FACE",FACE,{"disambiguationData":[OSD([sQuery(id+"F6.wireOp",EDGE,"E192.right")])]})});
            var sketch = newSketch(context, id + "F18", { "sketchPlane" : qUnion([Q0])});
            skCircle(sketch, "E202", {"center": v(0, 0) * mm, "radius": 65 * mm});
            skSolve(sketch);
        }
        {
            var Q0;
            Q0=makeQuery(id+"F18.imprint","IMPRINT",FACE,{"disambiguationData":[TD([[makeQuery(id+"F18.imprint","IMPRINT",EDGE,{"derivedFrom":sQuery(id+"F18.wireOp",EDGE,"E202")}),1.0]])]});
            extrude(context, id + "F19", {"entities" : qUnion([Q0]), "operationType" : NewBodyOperationType.REMOVE, "oppositeDirection" : true, "depth" : 5 * mm, "offsetDistance" : 25 * mm});
        }
    });
